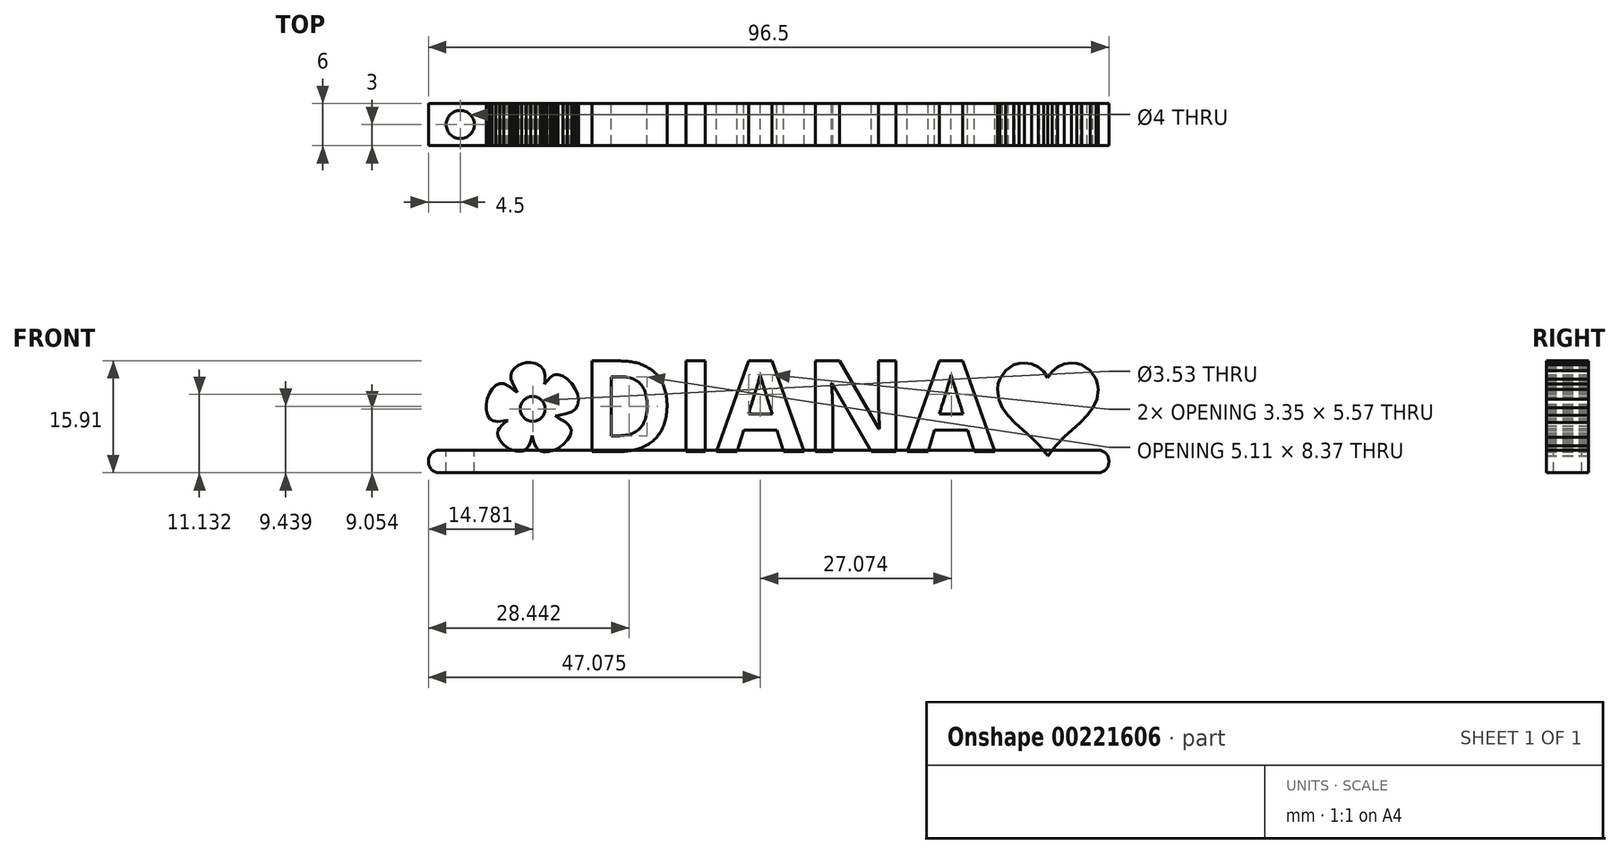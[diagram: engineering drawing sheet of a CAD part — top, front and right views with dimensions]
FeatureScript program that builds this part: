
annotation { "Feature Type Name" : "Feature", "Feature Type Description" : "" }
export const myFeature = defineFeature(function(context is Context, id is Id, definition is map)
    precondition{}
    {
        {
            var Q0;
            Q0=qCreatedBy(makeId("Front.planeOp"),FACE);
            var sketch = newSketch(context, id + "F0", { "sketchPlane" : qUnion([Q0])});
            skText(sketch, "E0", { "text": "   DIANA", "fontName": "OpenSans-Bold.ttf"});
            skLineSegment(sketch, "E1.0.0", {"start": v(-9.3, 0.1) * mm, "end": v(-8.53, 0.46) * mm});
            skLineSegment(sketch, "E1.0.1", {"start": v(-8.53, 0.46) * mm, "end": v(-7.79, 1.02) * mm});
            skLineSegment(sketch, "E1.0.2", {"start": v(-7.79, 1.02) * mm, "end": v(-7.18, 1.67) * mm});
            skLineSegment(sketch, "E1.0.3", {"start": v(-7.18, 1.67) * mm, "end": v(-6.78, 2.35) * mm});
            skLineSegment(sketch, "E1.0.4", {"start": v(-6.78, 2.35) * mm, "end": v(-6.68, 2.7) * mm});
            skLineSegment(sketch, "E1.0.5", {"start": v(-6.68, 2.7) * mm, "end": v(-6.67, 3.02) * mm});
            skLineSegment(sketch, "E1.0.6", {"start": v(-6.67, 3.02) * mm, "end": v(-6.73, 3.33) * mm});
            skLineSegment(sketch, "E1.0.7", {"start": v(-6.73, 3.33) * mm, "end": v(-6.89, 3.62) * mm});
            skLineSegment(sketch, "E1.0.8", {"start": v(-6.89, 3.62) * mm, "end": v(-7.48, 4.2) * mm});
            skLineSegment(sketch, "E1.0.9", {"start": v(-7.48, 4.2) * mm, "end": v(-8.5, 4.79) * mm});
            skLineSegment(sketch, "E1.0.10", {"start": v(-8.5, 4.79) * mm, "end": v(-8.93, 5.06) * mm});
            skLineSegment(sketch, "E1.0.11", {"start": v(-8.93, 5.06) * mm, "end": v(-8.42, 5.16) * mm});
            skLineSegment(sketch, "E1.0.12", {"start": v(-8.42, 5.16) * mm, "end": v(-7.31, 5.37) * mm});
            skLineSegment(sketch, "E1.0.13", {"start": v(-7.31, 5.37) * mm, "end": v(-6.55, 5.65) * mm});
            skLineSegment(sketch, "E1.0.14", {"start": v(-6.55, 5.65) * mm, "end": v(-6.05, 6.04) * mm});
            skLineSegment(sketch, "E1.0.15", {"start": v(-6.05, 6.04) * mm, "end": v(-5.76, 6.58) * mm});
            skLineSegment(sketch, "E1.0.16", {"start": v(-5.76, 6.58) * mm, "end": v(-5.64, 7.33) * mm});
            skLineSegment(sketch, "E1.0.17", {"start": v(-5.64, 7.33) * mm, "end": v(-5.78, 8.14) * mm});
            skLineSegment(sketch, "E1.0.18", {"start": v(-5.78, 8.14) * mm, "end": v(-6.1, 8.93) * mm});
            skLineSegment(sketch, "E1.0.19", {"start": v(-6.1, 8.93) * mm, "end": v(-6.6, 9.67) * mm});
            skLineSegment(sketch, "E1.0.20", {"start": v(-6.6, 9.67) * mm, "end": v(-7.2, 10.28) * mm});
            skLineSegment(sketch, "E1.0.21", {"start": v(-7.2, 10.28) * mm, "end": v(-7.86, 10.72) * mm});
            skLineSegment(sketch, "E1.0.22", {"start": v(-7.86, 10.72) * mm, "end": v(-8.55, 10.93) * mm});
            skLineSegment(sketch, "E1.0.23", {"start": v(-8.55, 10.93) * mm, "end": v(-8.88, 10.93) * mm});
            skLineSegment(sketch, "E1.0.24", {"start": v(-8.88, 10.93) * mm, "end": v(-9.2, 10.85) * mm});
            skLineSegment(sketch, "E1.0.25", {"start": v(-9.2, 10.85) * mm, "end": v(-9.65, 10.56) * mm});
            skLineSegment(sketch, "E1.0.26", {"start": v(-9.65, 10.56) * mm, "end": v(-10.14, 9.98) * mm});
            skLineSegment(sketch, "E1.0.27", {"start": v(-10.14, 9.98) * mm, "end": v(-10.45, 9.58) * mm});
            skLineSegment(sketch, "E1.0.28", {"start": v(-10.45, 9.58) * mm, "end": v(-10.4, 10.03) * mm});
            skLineSegment(sketch, "E1.0.29", {"start": v(-10.4, 10.03) * mm, "end": v(-10.4, 10.93) * mm});
            skLineSegment(sketch, "E1.0.30", {"start": v(-10.4, 10.93) * mm, "end": v(-10.6, 11.63) * mm});
            skLineSegment(sketch, "E1.0.31", {"start": v(-10.6, 11.63) * mm, "end": v(-11.04, 12.15) * mm});
            skLineSegment(sketch, "E1.0.32", {"start": v(-11.04, 12.15) * mm, "end": v(-11.71, 12.5) * mm});
            skLineSegment(sketch, "E1.0.33", {"start": v(-11.71, 12.5) * mm, "end": v(-12.4, 12.64) * mm});
            skLineSegment(sketch, "E1.0.34", {"start": v(-12.4, 12.64) * mm, "end": v(-13.07, 12.62) * mm});
            skLineSegment(sketch, "E1.0.35", {"start": v(-13.07, 12.62) * mm, "end": v(-13.7, 12.47) * mm});
            skLineSegment(sketch, "E1.0.36", {"start": v(-13.7, 12.47) * mm, "end": v(-14.26, 12.2) * mm});
            skLineSegment(sketch, "E1.0.37", {"start": v(-14.26, 12.2) * mm, "end": v(-14.72, 11.83) * mm});
            skLineSegment(sketch, "E1.0.38", {"start": v(-14.72, 11.83) * mm, "end": v(-15.05, 11.38) * mm});
            skLineSegment(sketch, "E1.0.39", {"start": v(-15.05, 11.38) * mm, "end": v(-15.22, 10.87) * mm});
            skLineSegment(sketch, "E1.0.40", {"start": v(-15.22, 10.87) * mm, "end": v(-15.2, 10.3) * mm});
            skLineSegment(sketch, "E1.0.41", {"start": v(-15.2, 10.3) * mm, "end": v(-14.83, 9.4) * mm});
            skLineSegment(sketch, "E1.0.42", {"start": v(-14.83, 9.4) * mm, "end": v(-14.35, 8.55) * mm});
            skLineSegment(sketch, "E1.0.43", {"start": v(-14.35, 8.55) * mm, "end": v(-14.3, 8.4) * mm});
            skLineSegment(sketch, "E1.0.44", {"start": v(-14.3, 8.4) * mm, "end": v(-14.48, 8.53) * mm});
            skLineSegment(sketch, "E1.0.45", {"start": v(-14.48, 8.53) * mm, "end": v(-15.4, 9.23) * mm});
            skLineSegment(sketch, "E1.0.46", {"start": v(-15.4, 9.23) * mm, "end": v(-16.22, 9.63) * mm});
            skLineSegment(sketch, "E1.0.47", {"start": v(-16.22, 9.63) * mm, "end": v(-16.8, 9.63) * mm});
            skLineSegment(sketch, "E1.0.48", {"start": v(-16.8, 9.63) * mm, "end": v(-17.36, 9.37) * mm});
            skLineSegment(sketch, "E1.0.49", {"start": v(-17.36, 9.37) * mm, "end": v(-17.85, 8.9) * mm});
            skLineSegment(sketch, "E1.0.50", {"start": v(-17.85, 8.9) * mm, "end": v(-18.26, 8.26) * mm});
            skLineSegment(sketch, "E1.0.51", {"start": v(-18.26, 8.26) * mm, "end": v(-18.56, 7.51) * mm});
            skLineSegment(sketch, "E1.0.52", {"start": v(-18.56, 7.51) * mm, "end": v(-18.72, 6.71) * mm});
            skLineSegment(sketch, "E1.0.53", {"start": v(-18.72, 6.71) * mm, "end": v(-18.72, 5.9) * mm});
            skLineSegment(sketch, "E1.0.54", {"start": v(-18.72, 5.9) * mm, "end": v(-18.52, 5.16) * mm});
            skLineSegment(sketch, "E1.0.55", {"start": v(-18.52, 5.16) * mm, "end": v(-18.2, 4.64) * mm});
            skLineSegment(sketch, "E1.0.56", {"start": v(-18.2, 4.64) * mm, "end": v(-17.75, 4.36) * mm});
            skLineSegment(sketch, "E1.0.57", {"start": v(-17.75, 4.36) * mm, "end": v(-17.1, 4.27) * mm});
            skLineSegment(sketch, "E1.0.58", {"start": v(-17.1, 4.27) * mm, "end": v(-16.21, 4.37) * mm});
            skLineSegment(sketch, "E1.0.59", {"start": v(-16.21, 4.37) * mm, "end": v(-15.7, 4.43) * mm});
            skLineSegment(sketch, "E1.0.60", {"start": v(-15.7, 4.43) * mm, "end": v(-15.67, 4.4) * mm});
            skLineSegment(sketch, "E1.0.61", {"start": v(-15.67, 4.4) * mm, "end": v(-15.78, 4.33) * mm});
            skLineSegment(sketch, "E1.0.62", {"start": v(-15.78, 4.33) * mm, "end": v(-16.17, 4.07) * mm});
            skLineSegment(sketch, "E1.0.63", {"start": v(-16.17, 4.07) * mm, "end": v(-16.55, 3.71) * mm});
            skLineSegment(sketch, "E1.0.64", {"start": v(-16.55, 3.71) * mm, "end": v(-16.87, 3.33) * mm});
            skLineSegment(sketch, "E1.0.65", {"start": v(-16.87, 3.33) * mm, "end": v(-17.04, 3) * mm});
            skLineSegment(sketch, "E1.0.66", {"start": v(-17.04, 3) * mm, "end": v(-17.08, 2.6) * mm});
            skLineSegment(sketch, "E1.0.67", {"start": v(-17.08, 2.6) * mm, "end": v(-17.02, 2.2) * mm});
            skLineSegment(sketch, "E1.0.68", {"start": v(-17.02, 2.2) * mm, "end": v(-16.87, 1.78) * mm});
            skLineSegment(sketch, "E1.0.69", {"start": v(-16.87, 1.78) * mm, "end": v(-16.62, 1.39) * mm});
            skLineSegment(sketch, "E1.0.70", {"start": v(-16.62, 1.39) * mm, "end": v(-16.3, 1.02) * mm});
            skLineSegment(sketch, "E1.0.71", {"start": v(-16.3, 1.02) * mm, "end": v(-15.9, 0.69) * mm});
            skLineSegment(sketch, "E1.0.72", {"start": v(-15.9, 0.69) * mm, "end": v(-15.45, 0.4) * mm});
            skLineSegment(sketch, "E1.0.73", {"start": v(-15.45, 0.4) * mm, "end": v(-14.95, 0.2) * mm});
            skLineSegment(sketch, "E1.0.74", {"start": v(-14.95, 0.2) * mm, "end": v(-14.44, 0.06) * mm});
            skLineSegment(sketch, "E1.0.75", {"start": v(-14.44, 0.06) * mm, "end": v(-13.98, 0.02) * mm});
            skLineSegment(sketch, "E1.0.76", {"start": v(-13.98, 0.02) * mm, "end": v(-13.58, 0.08) * mm});
            skLineSegment(sketch, "E1.0.77", {"start": v(-13.58, 0.08) * mm, "end": v(-13.23, 0.23) * mm});
            skLineSegment(sketch, "E1.0.78", {"start": v(-13.23, 0.23) * mm, "end": v(-12.92, 0.49) * mm});
            skLineSegment(sketch, "E1.0.79", {"start": v(-12.92, 0.49) * mm, "end": v(-12.67, 0.84) * mm});
            skLineSegment(sketch, "E1.0.80", {"start": v(-12.67, 0.84) * mm, "end": v(-12.46, 1.28) * mm});
            skLineSegment(sketch, "E1.0.81", {"start": v(-12.46, 1.28) * mm, "end": v(-12.3, 1.83) * mm});
            skLineSegment(sketch, "E1.0.82", {"start": v(-12.3, 1.83) * mm, "end": v(-12.19, 2.26) * mm});
            skLineSegment(sketch, "E1.0.83", {"start": v(-12.19, 2.26) * mm, "end": v(-12.13, 2.1) * mm});
            skLineSegment(sketch, "E1.0.84", {"start": v(-12.13, 2.1) * mm, "end": v(-12.01, 1.53) * mm});
            skLineSegment(sketch, "E1.0.85", {"start": v(-12.01, 1.53) * mm, "end": v(-11.82, 1) * mm});
            skLineSegment(sketch, "E1.0.86", {"start": v(-11.82, 1) * mm, "end": v(-11.6, 0.55) * mm});
            skLineSegment(sketch, "E1.0.87", {"start": v(-11.6, 0.55) * mm, "end": v(-11.35, 0.26) * mm});
            skLineSegment(sketch, "E1.0.88", {"start": v(-11.35, 0.26) * mm, "end": v(-10.95, 0.05) * mm});
            skLineSegment(sketch, "E1.0.89", {"start": v(-10.95, 0.05) * mm, "end": v(-10.46, -0.04) * mm});
            skLineSegment(sketch, "E1.0.90", {"start": v(-10.46, -0.04) * mm, "end": v(-9.9, -0.03) * mm});
            skLineSegment(sketch, "E1.0.91", {"start": v(-9.9, -0.03) * mm, "end": v(-9.3, 0.1) * mm});
            skCircle(sketch, "E2", {"center": v(-12.12, 6.05) * mm, "radius": 1.77 * mm});
            skLineSegment(sketch, "E3", {"start": v(57.6, 12.6) * mm, "end": v(56.84, 12.52) * mm});
            skLineSegment(sketch, "E4", {"start": v(56.84, 12.52) * mm, "end": v(56.13, 12.3) * mm});
            skLineSegment(sketch, "E5", {"start": v(56.13, 12.3) * mm, "end": v(54.94, 11.5) * mm});
            skLineSegment(sketch, "E6", {"start": v(54.94, 11.5) * mm, "end": v(54.13, 10.3) * mm});
            skLineSegment(sketch, "E7", {"start": v(54.13, 10.3) * mm, "end": v(53.9, 9.59) * mm});
            skLineSegment(sketch, "E8", {"start": v(53.9, 9.59) * mm, "end": v(53.83, 8.83) * mm});
            skLineSegment(sketch, "E9", {"start": v(53.83, 8.83) * mm, "end": v(54.02, 7.39) * mm});
            skLineSegment(sketch, "E10", {"start": v(54.02, 7.39) * mm, "end": v(54.54, 6.16) * mm});
            skLineSegment(sketch, "E11", {"start": v(54.54, 6.16) * mm, "end": v(55.33, 5.08) * mm});
            skLineSegment(sketch, "E12", {"start": v(55.33, 5.08) * mm, "end": v(56.31, 4.08) * mm});
            skLineSegment(sketch, "E13", {"start": v(56.31, 4.08) * mm, "end": v(58.6, 2.03) * mm});
            skLineSegment(sketch, "E14", {"start": v(58.6, 2.03) * mm, "end": v(59.8, 0.82) * mm});
            skLineSegment(sketch, "E15", {"start": v(59.8, 0.82) * mm, "end": v(60.92, -0.59) * mm});
            skLineSegment(sketch, "E16", {"start": v(60.92, -0.59) * mm, "end": v(60.96, -0.65) * mm});
            skLineSegment(sketch, "E17", {"start": v(60.96, -0.65) * mm, "end": v(61, -0.59) * mm});
            skLineSegment(sketch, "E18", {"start": v(61, -0.59) * mm, "end": v(62.08, 0.82) * mm});
            skLineSegment(sketch, "E19", {"start": v(62.08, 0.82) * mm, "end": v(63.24, 2.03) * mm});
            skLineSegment(sketch, "E20", {"start": v(63.24, 2.03) * mm, "end": v(65.55, 4.12) * mm});
            skLineSegment(sketch, "E21", {"start": v(65.55, 4.12) * mm, "end": v(66.55, 5.13) * mm});
            skLineSegment(sketch, "E22", {"start": v(66.55, 5.13) * mm, "end": v(67.35, 6.21) * mm});
            skLineSegment(sketch, "E23", {"start": v(67.35, 6.21) * mm, "end": v(67.89, 7.42) * mm});
            skLineSegment(sketch, "E24", {"start": v(67.89, 7.42) * mm, "end": v(68.08, 8.83) * mm});
            skLineSegment(sketch, "E25", {"start": v(68.08, 8.83) * mm, "end": v(68, 9.59) * mm});
            skLineSegment(sketch, "E26", {"start": v(68, 9.59) * mm, "end": v(67.79, 10.3) * mm});
            skLineSegment(sketch, "E27", {"start": v(67.79, 10.3) * mm, "end": v(66.98, 11.5) * mm});
            skLineSegment(sketch, "E28", {"start": v(66.98, 11.5) * mm, "end": v(65.78, 12.3) * mm});
            skLineSegment(sketch, "E29", {"start": v(65.78, 12.3) * mm, "end": v(65.08, 12.52) * mm});
            skLineSegment(sketch, "E30", {"start": v(65.08, 12.52) * mm, "end": v(64.32, 12.6) * mm});
            skLineSegment(sketch, "E31", {"start": v(64.32, 12.6) * mm, "end": v(63.26, 12.44) * mm});
            skLineSegment(sketch, "E32", {"start": v(63.26, 12.44) * mm, "end": v(62.32, 12.01) * mm});
            skLineSegment(sketch, "E33", {"start": v(62.32, 12.01) * mm, "end": v(61.54, 11.35) * mm});
            skLineSegment(sketch, "E34", {"start": v(61.54, 11.35) * mm, "end": v(60.96, 10.5) * mm});
            skLineSegment(sketch, "E35", {"start": v(60.96, 10.5) * mm, "end": v(60.38, 11.35) * mm});
            skLineSegment(sketch, "E36", {"start": v(60.38, 11.35) * mm, "end": v(59.6, 12.01) * mm});
            skLineSegment(sketch, "E37", {"start": v(59.6, 12.01) * mm, "end": v(58.66, 12.44) * mm});
            skLineSegment(sketch, "E38", {"start": v(58.66, 12.44) * mm, "end": v(57.6, 12.6) * mm});
            skLineSegment(sketch, "E39", {"start": v(54.6, 12.97) * mm, "end": v(73.83, 12.97) * mm, "construction": true});
            const initialGuessF0  = {"E0": [-0.0194, 0, 1, 0, 0.01297]};
            skSetInitialGuess(sketch, initialGuessF0);
            skSolve(sketch);
        }
        {
            var Q0;
            Q0=qSketchRegion(id+"F0",true);
            extrude(context, id + "F1", {"entities" : qUnion([Q0]), "endBound" : BoundingType.SYMMETRIC, "depth" : 6 * mm});
        }
        {
            var Q0;
            Q0=qCreatedBy(makeId("Top.planeOp"),FACE);
            var sketch = newSketch(context, id + "F2", { "sketchPlane" : qUnion([Q0])});
            skLineSegment(sketch, "E40.bottom", {"start": v(-19.4, 3) * mm, "end": v(69.6, 3) * mm});
            skLineSegment(sketch, "E40.top", {"start": v(-19.4, -3) * mm, "end": v(69.6, -3) * mm});
            skLineSegment(sketch, "E40.left", {"start": v(-19.4, 3) * mm, "end": v(-19.4, -3) * mm});
            skLineSegment(sketch, "E40.right", {"start": v(69.6, 3) * mm, "end": v(69.6, -3) * mm});
            skSolve(sketch);
        }
        {
            var Q0;
            Q0=makeQuery(id+"F2.imprint","IMPRINT",FACE,{"disambiguationData":[TD([[makeQuery(id+"F2.imprint","IMPRINT",EDGE,{"derivedFrom":sQuery(id+"F2.wireOp",EDGE,"E40.bottom")}),-1.0]])]});
            extrude(context, id + "F3", {"entities" : qUnion([Q0]), "depth" : 0.2 * mm});
        }
        {
            var Q0;
            Q0=makeQuery(id+"F3.opExtrude","CAP_FACE",FACE,{"disambiguationData":[OSD([sQuery(id+"F2.wireOp",EDGE,"E40.bottom"),sQuery(id+"F2.wireOp",EDGE,"E40.top"),sQuery(id+"F2.wireOp",EDGE,"E40.left"),sQuery(id+"F2.wireOp",EDGE,"E40.right")])],"isStart":true});
            extrude(context, id + "F4", {"entities" : qUnion([Q0]), "depth" : 3 * mm});
        }
        {
            var Q0;
            {var subQ0=sQuery(id+"F2.wireOp",EDGE,"E40.left");Q0=makeQuery(id+"FaVoHrOpcFZXiYX_6.opBoolean","MERGE",FACE,{"derivedFrom":[makeQuery(id+"F3.opExtrude","SWEPT_FACE",FACE,{"disambiguationData":[OSD([subQ0])]}),makeQuery(id+"F4.opExtrude","SWEPT_FACE",FACE,{"disambiguationData":[OSD([subQ0])]})]});}
            var sketch = newSketch(context, id + "F5", { "sketchPlane" : qUnion([Q0])});
            skLineSegment(sketch, "E41.bottom", {"start": v(-3, -3) * mm, "end": v(3, -3) * mm});
            skLineSegment(sketch, "E41.top", {"start": v(-3, 0.2) * mm, "end": v(3, 0.2) * mm});
            skLineSegment(sketch, "E41.left", {"start": v(-3, -3) * mm, "end": v(-3, 0.2) * mm});
            skLineSegment(sketch, "E41.right", {"start": v(3, -3) * mm, "end": v(3, 0.2) * mm});
            skSolve(sketch);
        }
        {
            var Q0;
            Q0=qSketchRegion(id+"F5",true);
            extrude(context, id + "F6", {"entities" : qUnion([Q0]), "operationType" : NewBodyOperationType.ADD, "depth" : 7.5 * mm});
        }
        {
            var Q0;
            Q0=makeQuery(id+"F6.opExtrude","CAP_EDGE",EDGE,{"disambiguationData":[OSD([sQuery(id+"F5.wireOp",EDGE,"E41.bottom")])],"isStart":false});
            var Q1;
            Q1=makeQuery(id+"F6.opExtrude","CAP_EDGE",EDGE,{"disambiguationData":[OSD([sQuery(id+"F5.wireOp",EDGE,"E41.top")])],"isStart":false});
            var Q2;
            Q2=makeQuery(id+"F4.opExtrude","CAP_EDGE",EDGE,{"disambiguationData":[OSD([sQuery(id+"F2.wireOp",EDGE,"E40.right")])],"isStart":false});
            fillet(context, id + "F7", {"entities" : qUnion([Q0, Q1, Q2]), "radius" : 1.5 * mm, "tangentPropagation" : true, "allowEdgeOverflow" : false});
        }
        {
            var Q0;
            {var subQ19=sQuery(id+"F2.wireOp",EDGE,"E40.top");var subQ20=sQuery(id+"F2.wireOp",EDGE,"E40.bottom");var subQ63=sQuery(id+"F0.wireOp",EDGE,"E0.sketch_text.stroke-2");var subQ66=sQuery(id+"F2.wireOp",EDGE,"E40.left");Q0=makeQuery(id+"F6.boolean.opBoolean","MERGE",FACE,{"derivedFrom":[makeQuery(id+"FaVoHrOpcFZXiYX_6.opBoolean","SPLIT",FACE,{"disambiguationData":[TD([makeQuery(id+"F1.opExtrude","SWEPT_FACE",FACE,{"disambiguationData":[OSD([subQ63])]})])],"derivedFrom":makeQuery(id+"F3.opExtrude","CAP_FACE",FACE,{"disambiguationData":[OSD([subQ20,subQ19,subQ66,sQuery(id+"F2.wireOp",EDGE,"E40.right")])],"isStart":false})}),makeQuery(id+"F6.opExtrude","SWEPT_FACE",FACE,{"disambiguationData":[OSD([sQuery(id+"F5.wireOp",EDGE,"E41.top")])]})]});}
            var sketch = newSketch(context, id + "F8", { "sketchPlane" : qUnion([Q0])});
            skCircle(sketch, "E42", {"center": v(-22.4, 0) * mm, "radius": 2 * mm});
            skSolve(sketch);
        }
        {
            var Q0;
            Q0=makeQuery(id+"F8.imprint","IMPRINT",FACE,{"disambiguationData":[TD([[makeQuery(id+"F8.imprint","IMPRINT",EDGE,{"derivedFrom":sQuery(id+"F8.wireOp",EDGE,"E42")}),1.0]])]});
            extrude(context, id + "F9", {"entities" : qUnion([Q0]), "operationType" : NewBodyOperationType.REMOVE, "oppositeDirection" : true, "depth" : 4 * mm});
        }
        {
            var Q0;
            Q0=makeQuery(id+"F3.opExtrude","CAP_EDGE",EDGE,{"disambiguationData":[OSD([sQuery(id+"F2.wireOp",EDGE,"E40.right")])],"isStart":false});
            fillet(context, id + "F10", {"entities" : qUnion([Q0]), "radius" : 1.5 * mm, "tangentPropagation" : true, "allowEdgeOverflow" : false});
        }
    });
